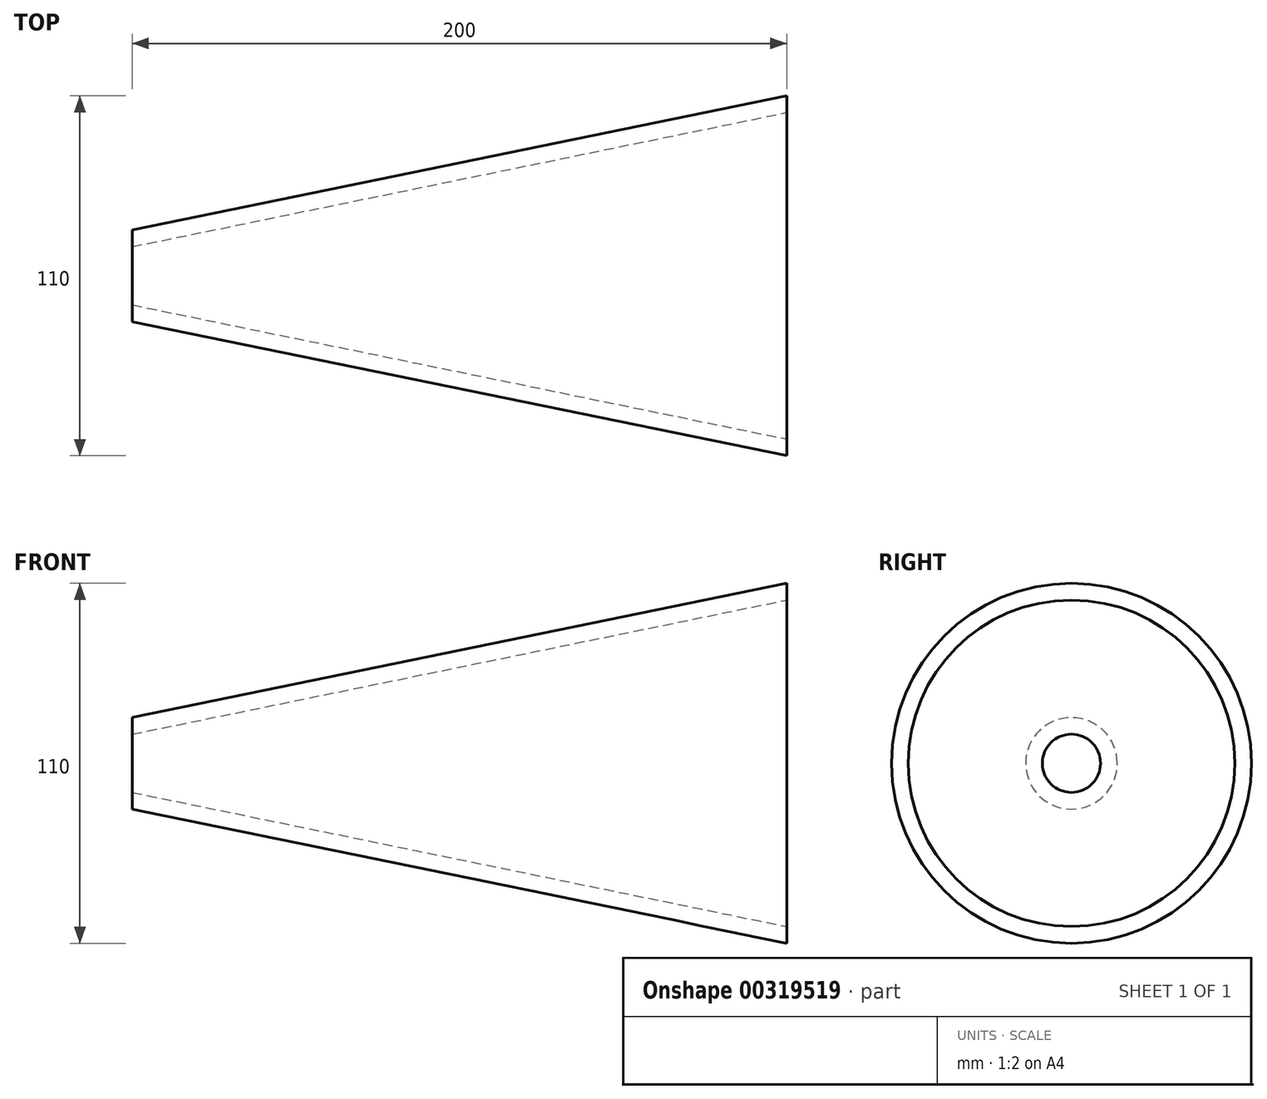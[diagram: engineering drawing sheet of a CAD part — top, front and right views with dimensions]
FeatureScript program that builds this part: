
annotation { "Feature Type Name" : "Feature", "Feature Type Description" : "" }
export const myFeature = defineFeature(function(context is Context, id is Id, definition is map)
    precondition{}
    {
        {
            var Q0;
            Q0=qCreatedBy(makeId("Right.planeOp"),FACE);
            cPlane(context, id + "F0", {"entities" : qUnion([Q0]), "cplaneType" : CPlaneType.OFFSET, "offset" : 200 * mm, "width" : 150 * mm, "height" : 150 * mm});
        }
        {
            var Q0;
            Q0=qCreatedBy(makeId("Right.planeOp"),FACE);
            var sketch = newSketch(context, id + "F1", { "sketchPlane" : qUnion([Q0])});
            skCircle(sketch, "E0", {"center": v(0, 0) * mm, "radius": 14 * mm});
            skSolve(sketch);
        }
        {
            var Q0;
            Q0=qCreatedBy(id+"F0.planeOp",FACE);
            var sketch = newSketch(context, id + "F2", { "sketchPlane" : qUnion([Q0])});
            skCircle(sketch, "E1", {"center": v(0, 0) * mm, "radius": 55 * mm});
            skSolve(sketch);
        }
        {
            var Q0;
            Q0=makeQuery(id+"F1.imprint","IMPRINT",FACE,{"disambiguationData":[TD([[makeQuery(id+"F1.imprint","IMPRINT",EDGE,{"derivedFrom":sQuery(id+"F1.wireOp",EDGE,"E0")}),1.0]])]});
            var Q1;
            Q1=makeQuery(id+"F2.imprint","IMPRINT",FACE,{"disambiguationData":[TD([[makeQuery(id+"F2.imprint","IMPRINT",EDGE,{"derivedFrom":sQuery(id+"F2.wireOp",EDGE,"E1")}),1.0]])]});
            loft(context, id + "F3", {"sheetProfilesArray" : [{ "sheetProfileEntities" : qUnion([Q0]) }, { "sheetProfileEntities" : qUnion([Q1]) }]});
        }
        {
            var Q0;
            Q0=makeQuery(id+"F3.opLoft","CAP_FACE",FACE,{"disambiguationData":[OSD([makeQuery(id+"F2.imprint","IMPRINT",FACE,{"disambiguationData":[TD([[makeQuery(id+"F2.imprint","IMPRINT",EDGE,{"derivedFrom":sQuery(id+"F2.wireOp",EDGE,"E1")}),1.0]])]})])],"isStart":true});
            var Q1;
            Q1=makeQuery(id+"F3.opLoft","CAP_FACE",FACE,{"disambiguationData":[OSD([makeQuery(id+"F1.imprint","IMPRINT",FACE,{"disambiguationData":[TD([[makeQuery(id+"F1.imprint","IMPRINT",EDGE,{"derivedFrom":sQuery(id+"F1.wireOp",EDGE,"E0")}),1.0]])]})])],"isStart":true});
            shell(context, id + "F4", {"entities" : qUnion([Q0, Q1]), "thickness" : 5 * mm});
        }
    });
